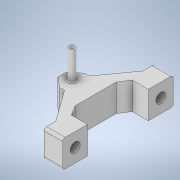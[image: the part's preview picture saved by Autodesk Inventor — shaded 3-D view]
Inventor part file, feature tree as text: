
AUTODESK INVENTOR PART (.ipt)
format: ipt  version: 2022 (Build 260153000, 153)  size: 396,288 bytes
history: native  units: mm
features: extrude x8, sketch x7, chamfer x5, hole x2, other x1, fillet x1
ambient origin geometry x8: Origin, YZ Plane, XZ Plane, XY Plane, X Axis, Y Axis, Z Axis, Center Point
bodies: Body1 (feature_tree)
feature tree (24):
  other  "Sólido1"
  extrude  "Extrusão1"  Depth=22.0mm
  hole  "Furo1"  [1 undecoded]
  extrude  "Extrusão2"  Depth=18.0mm TaperAngle=45.0deg
  chamfer  "Chanfro1"  Distance=18.0mm Angle=45.0deg
  hole  "Furo2"  [1 undecoded]
  chamfer  "Chanfro3"  Distance=10.0mm
  fillet  "Arredondamento2"  Radius=18.0mm
  extrude  "Extrusão5"  Depth=2.0mm TaperAngle=45.0deg
  chamfer  "Chanfro6"  Distance=5.0mm Angle=45.0deg
  chamfer  "Chanfro7"  Distance=3.0mm
  sketch  "Esboço12"  dims[d21=8.0mm d22=6.0mm d23=4.0mm d24=2.0mm d25=90.0deg d26=8.0mm d27=0.0mm]
  extrude  "Extrusão6"  Depth=2.0mm
  extrude  "Extrusão7"  Depth=2.0mm
  extrude  "Extrusão8"  Depth=2.0mm
  sketch  "Esboço13"  dims[d28=2.0mm d36=18.0mm d37=25.0mm d38=45.0deg d68=10.0mm d70=10.0mm d71=18.0mm d72=0.0mm d73=5.0mm d74=8.0mm d75=45.0deg d76=5.0mm d77=8.0mm d78=45.0deg d79=3.0mm d81=8.0mm d82=24.43461mm d83=24.43461mm d84=3.0mm d85=0.0mm d86=0.0mm d87=10.0mm d88=0.0mm d89=21.0mm d90=22.0mm d91=0.0mm d92=0.0mm d99=5.0mm d100=10.0mm d101=0.0mm d102=23.0mm d103=0.0mm d104=1.0mm d105=2.0mm d106=45.0deg d46=0.5mm d47=0.872665mm d48=0.5mm d49=0.872665mm d66=0.5mm d67=0.872665mm d69=0.872665mm]
  extrude  "Extrusão11"  Depth=3.0mm
  extrude  "Extrusão12"  TaperAngle=0.0deg  [1 undecoded]
  chamfer  "Chanfro8"  Distance=10.0mm
  sketch  "Esboço1"  dims[d0=22.0mm d1=22.0mm]
  sketch  "Esboço2"  dims[d2=20.0mm d3=0.0mm]
  sketch  "Esboço3"  dims[d4=15.0mm d5=6.0mm d6=4.0mm d7=2.0mm d8=90.0deg d9=7.5mm d10=0.0mm d13=15.0mm]
  sketch  "Esboço4"  dims[d14=0.0mm d15=0.0mm d16=18.0mm d17=25.0mm d18=45.0deg]
  sketch  "Esboço10"  dims[d20=10.0mm]
note: 3 required parameter values undecoded (feature->parameter linkage not recoverable at this tier; creation-order binding heuristic only, values carry confidence <= 0.55)
